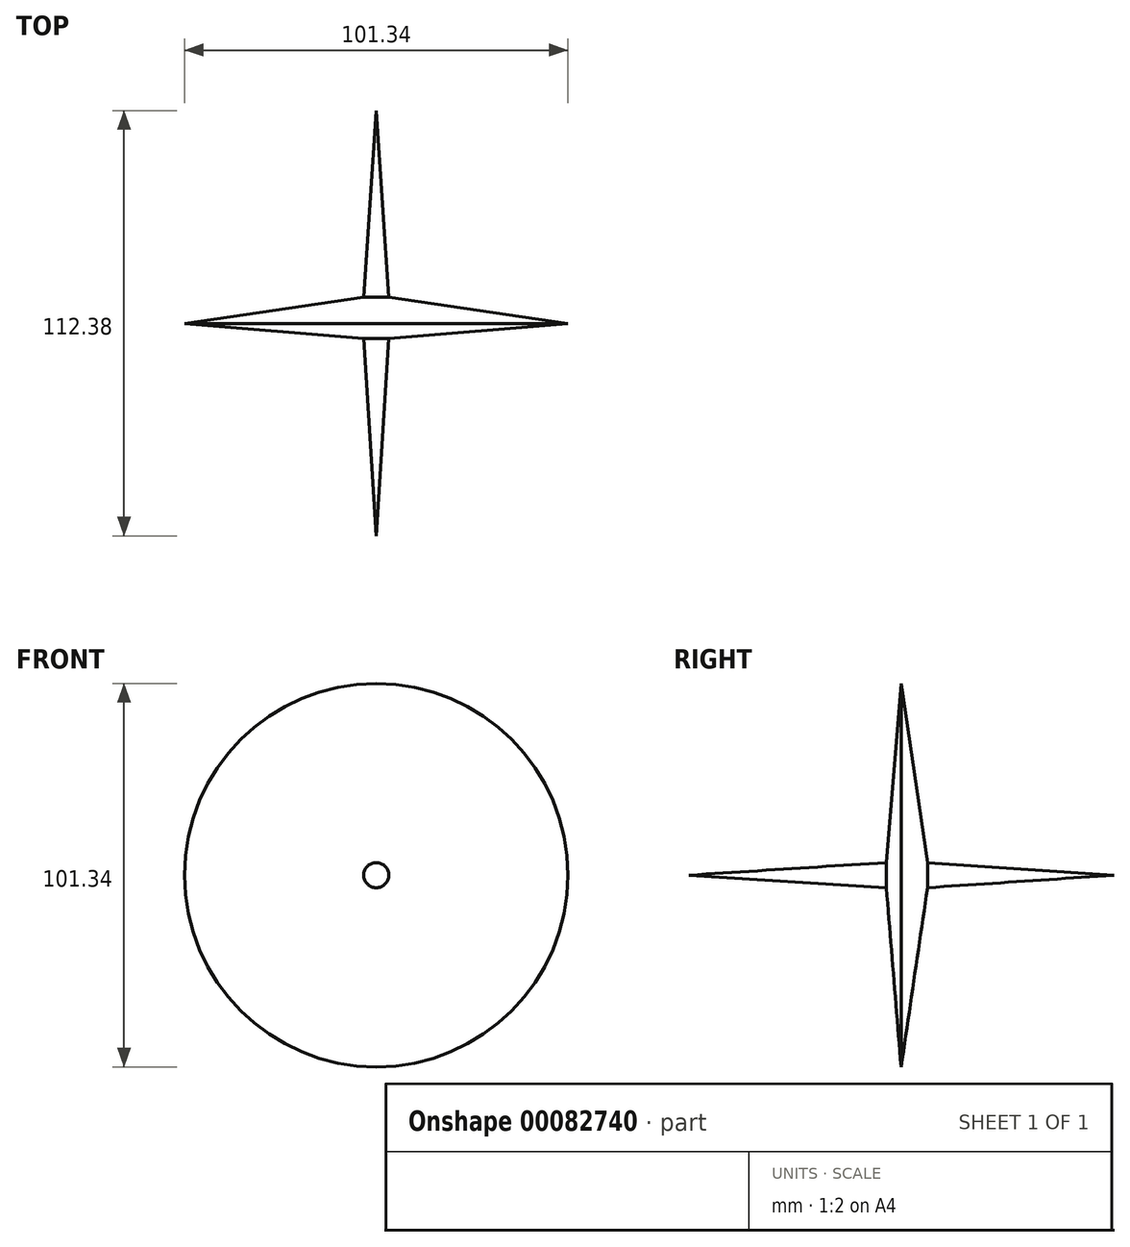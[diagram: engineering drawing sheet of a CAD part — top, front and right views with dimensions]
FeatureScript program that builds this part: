
annotation { "Feature Type Name" : "Feature", "Feature Type Description" : "" }
export const myFeature = defineFeature(function(context is Context, id is Id, definition is map)
    precondition{}
    {
        {
            var Q0;
            Q0=qCreatedBy(makeId("Top.planeOp"),FACE);
            var sketch = newSketch(context, id + "F0", { "sketchPlane" : qUnion([Q0])});
            skLineSegment(sketch, "E0", {"start": v(0, 56.26) * mm, "end": v(3.31, 6.97) * mm});
            skLineSegment(sketch, "E1", {"start": v(3.31, 6.97) * mm, "end": v(50.67, 0) * mm});
            skLineSegment(sketch, "E2", {"start": v(50.67, 0) * mm, "end": v(3.31, -3.93) * mm});
            skLineSegment(sketch, "E3", {"start": v(3.31, -3.93) * mm, "end": v(0, -56.12) * mm});
            skLineSegment(sketch, "E4", {"start": v(0, -56.12) * mm, "end": v(0, 56.26) * mm});
            skSolve(sketch);
        }
        {
            var Q0;
            Q0=makeQuery(id+"F0.imprint","IMPRINT",FACE,{"disambiguationData":[TD([[makeQuery(id+"F0.imprint","IMPRINT",EDGE,{"derivedFrom":sQuery(id+"F0.wireOp",EDGE,"E0")}),-1.0]])]});
            var Q1;
            Q1=sQuery(id+"F0.wireOp",EDGE,"E4");
            revolve(context, id + "F1", {"entities" : qUnion([Q0]), "axis" : qUnion([Q1]), "revolveType" : RevolveType.FULL});
        }
    });
